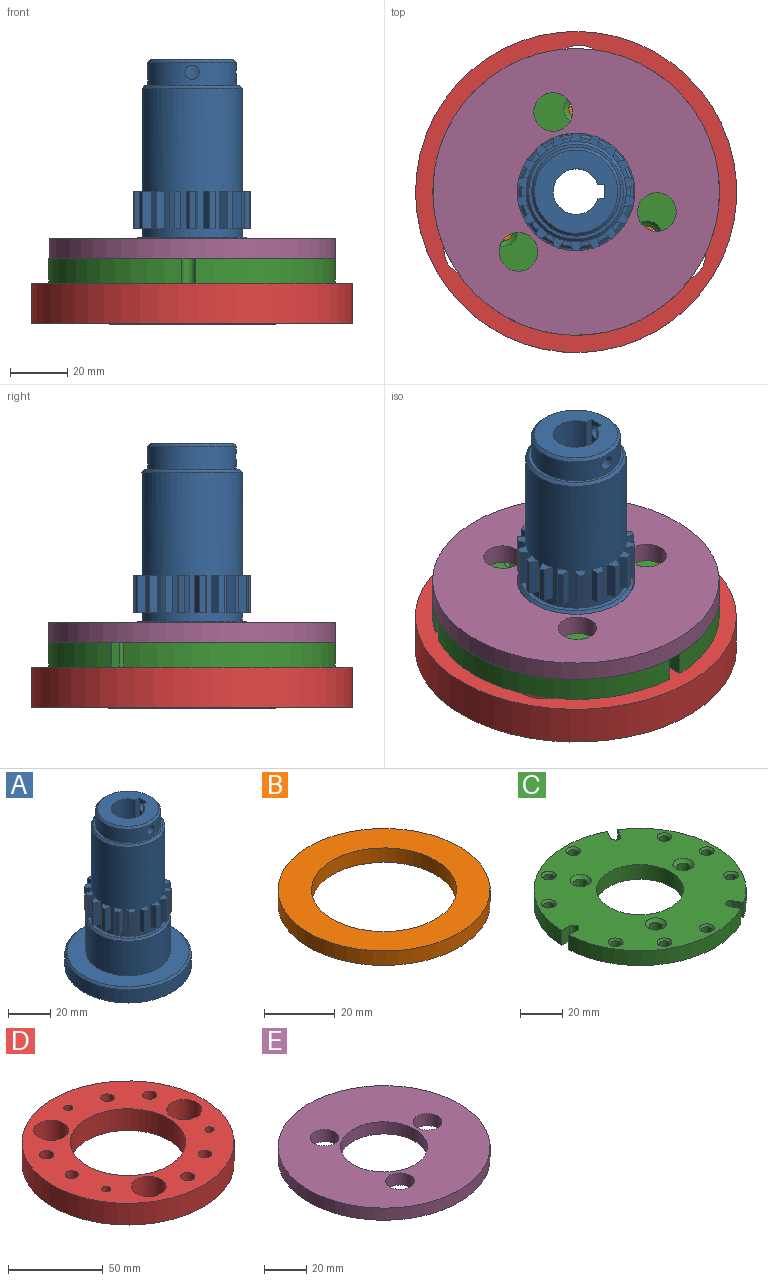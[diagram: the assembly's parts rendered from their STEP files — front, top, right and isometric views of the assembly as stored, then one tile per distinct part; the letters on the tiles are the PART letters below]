
ASSEMBLY  parts=5 mates=4
PART A: 113 faces, bbox 60x60x92.5 mm
  f0: cylinder r=15.5mm len=31mm, axis (0,0,1), area 739.9mm2, adj f4,f21,f22,f111
  f1: plane 59x5mm, normal (-1,0,0), area 285.2mm2, adj f6,f13,f14,f22
  f2: cylinder r=8mm len=63.5mm, axis (0,0,1), area 2849.1mm2, adj f5,f6,f13,f14,f21
  f3: cylinder r=17.5mm len=52mm, axis (0,0,1), area 4756.5mm2, adj f12,f16,f17,f18,f20,f23,f24,f25
  f4: plane 33x33mm, normal (0,0,1), area 100.5mm2, adj f0,f110
  f5: plane 29x29mm, normal (0,0,1), area 448.8mm2, adj f2,f13,f14,f15,f111
  f6: plane 26x26mm, normal (0,0,-1), area 319.2mm2, adj f1,f2,f7,f13,f14
  f7: cylinder r=13mm len=29mm, axis (0,0,1), area 2368.8mm2, adj f6,f8
  f8: plane 58x58mm, normal (0,0,-1), area 2111.2mm2, adj f7,f108
  f9: cylinder r=30mm len=60mm, axis (0,0,1), area 1413.7mm2, adj f108,f109
  f10: plane 58x58mm, normal (0,0,1), area 1385.4mm2, adj f11,f109
  f11: cylinder r=20mm len=40mm, axis (0,0,1), area 2513.3mm2, adj f10,f112
  f12: plane 38x38mm, normal (0,0,1), area 172mm2, adj f3,f112
  f13: plane 63.5x2.4mm, normal (0,-1,0), area 152.4mm2, adj f1,f2,f5,f6,f15
  f14: plane 63.5x2.4mm, normal (0,1,0), area 152.4mm2, adj f1,f2,f5,f6,f15
  f15: plane 5x4.5mm, normal (-1,0,0), area 12.7mm2, adj f5,f13,f14,f22
  f16: plane 4.04x3.59mm, normal (0,0,1), area 9.4mm2, adj f3,f17,f19,f20
  f17: plane 13x3.22mm, normal (0.13,-0.99,0), area 42.2mm2, adj f3,f16,f18,f19
  f18: plane 4.04x3.59mm, normal (0,0,-1), area 9.4mm2, adj f3,f17,f19,f20
  f19: cylinder r=20.5mm len=13mm, axis (0,0,-1), area 27.9mm2, adj f16,f17,f18,f20
  f20: plane 13x2.88mm, normal (0.46,0.89,0), area 42.2mm2, adj f3,f16,f18,f19
  f21: cylinder r=2.5mm len=7.9mm, axis (0,1,0), area 119.3mm2, adj f0,f2
  f22: cylinder r=2.5mm len=5.5mm, axis (-1,0,0), area 84.8mm2, adj f0,f1,f15
  f23: plane 4.25x4.24mm, normal (0,0,1), area 9.4mm2, adj f3,f24,f26,f27
  f24: plane 13x3.17mm, normal (-0.22,-0.98,0), area 42.2mm2, adj f3,f23,f25,f26
  f25: plane 4.25x4.24mm, normal (0,0,-1), area 9.4mm2, adj f3,f24,f26,f27
  f26: cylinder r=20.5mm len=13mm, axis (0,0,-1), area 27.9mm2, adj f23,f24,f25,f27
  f27: plane 13x2.39mm, normal (0.74,0.67,0), area 42.2mm2, adj f3,f23,f25,f26
  f28: plane 4.38x4.37mm, normal (0,0,1), area 9.4mm2, adj f3,f29,f31,f32
  f29: plane 13x2.74mm, normal (-0.54,-0.84,0), area 42.2mm2, adj f3,f28,f30,f31
  f30: plane 4.38x4.37mm, normal (0,0,-1), area 9.4mm2, adj f3,f29,f31,f32
  f31: cylinder r=20.5mm len=13mm, axis (0,0,-1), area 27.9mm2, adj f28,f29,f30,f32
  f32: plane 13x3mm, normal (0.92,0.38,0), area 42.2mm2, adj f3,f28,f30,f31
  f33: plane 3.99x3.97mm, normal (0,0,1), area 9.4mm2, adj f3,f34,f36,f37
  f34: plane 13x2.57mm, normal (-0.79,-0.61,0), area 42.2mm2, adj f3,f33,f35,f36
  f35: plane 3.99x3.97mm, normal (0,0,-1), area 9.4mm2, adj f3,f34,f36,f37
  f36: cylinder r=20.5mm len=13mm, axis (0,0,-1), area 27.9mm2, adj f33,f34,f35,f37
  f37: plane 13x3.24mm, normal (1,0.04,0), area 42.2mm2, adj f3,f33,f35,f36
  f38: plane 4.1x3.12mm, normal (0,0,1), area 9.4mm2, adj f3,f39,f41,f42
  f39: plane 13x3.09mm, normal (-0.95,-0.3,0), area 42.2mm2, adj f3,f38,f40,f41
  f40: plane 4.1x3.12mm, normal (0,0,-1), area 9.4mm2, adj f3,f39,f41,f42
  f41: cylinder r=20.5mm len=13mm, axis (0,0,-1), area 27.9mm2, adj f38,f39,f40,f42
  f42: plane 13x3.09mm, normal (0.95,-0.3,0), area 42.2mm2, adj f3,f38,f40,f41
  f43: plane 3.99x3.97mm, normal (0,0,1), area 9.4mm2, adj f3,f44,f46,f47
  f44: plane 13x3.24mm, normal (-1,0.04,0), area 42.2mm2, adj f3,f43,f45,f46
  f45: plane 3.99x3.97mm, normal (0,0,-1), area 9.4mm2, adj f3,f44,f46,f47
  f46: cylinder r=20.5mm len=13mm, axis (0,0,-1), area 27.9mm2, adj f43,f44,f45,f47
  f47: plane 13x2.57mm, normal (0.79,-0.61,0), area 42.2mm2, adj f3,f43,f45,f46
  f48: plane 4.38x4.37mm, normal (0,0,1), area 9.4mm2, adj f3,f49,f51,f52
  f49: plane 13x3mm, normal (-0.92,0.38,0), area 42.2mm2, adj f3,f48,f50,f51
  f50: plane 4.38x4.37mm, normal (0,0,-1), area 9.4mm2, adj f3,f49,f51,f52
  f51: cylinder r=20.5mm len=13mm, axis (0,0,-1), area 27.9mm2, adj f48,f49,f50,f52
  f52: plane 13x2.74mm, normal (0.54,-0.84,0), area 42.2mm2, adj f3,f48,f50,f51
  f53: plane 4.25x4.24mm, normal (0,0,1), area 9.4mm2, adj f3,f54,f56,f57
  f54: plane 13x2.39mm, normal (-0.74,0.67,0), area 42.2mm2, adj f3,f53,f55,f56
  f55: plane 4.25x4.24mm, normal (0,0,-1), area 9.4mm2, adj f3,f54,f56,f57
  f56: cylinder r=20.5mm len=13mm, axis (0,0,-1), area 27.9mm2, adj f53,f54,f55,f57
  f57: plane 13x3.17mm, normal (0.22,-0.98,0), area 42.2mm2, adj f3,f53,f55,f56
  f58: plane 4.04x3.59mm, normal (0,0,1), area 9.4mm2, adj f3,f59,f61,f62
  f59: plane 13x2.88mm, normal (-0.46,0.89,0), area 42.2mm2, adj f3,f58,f60,f61
  f60: plane 4.04x3.59mm, normal (0,0,-1), area 9.4mm2, adj f3,f59,f61,f62
  f61: cylinder r=20.5mm len=13mm, axis (0,0,-1), area 27.9mm2, adj f58,f59,f60,f62
  f62: plane 13x3.22mm, normal (-0.13,-0.99,0), area 42.2mm2, adj f3,f58,f60,f61
  f63: plane 4.04x3.59mm, normal (0,0,1), area 9.4mm2, adj f3,f64,f66,f67
  f64: plane 13x3.22mm, normal (-0.13,0.99,0), area 42.2mm2, adj f3,f63,f65,f66
  f65: plane 4.04x3.59mm, normal (0,0,-1), area 9.4mm2, adj f3,f64,f66,f67
  f66: cylinder r=20.5mm len=13mm, axis (0,0,-1), area 27.9mm2, adj f63,f64,f65,f67
  f67: plane 13x2.88mm, normal (-0.46,-0.89,0), area 42.2mm2, adj f3,f63,f65,f66
  f68: plane 4.25x4.24mm, normal (0,0,1), area 9.4mm2, adj f3,f69,f71,f72
  f69: plane 13x3.17mm, normal (0.22,0.98,0), area 42.2mm2, adj f3,f68,f70,f71
  f70: plane 4.25x4.24mm, normal (0,0,-1), area 9.4mm2, adj f3,f69,f71,f72
  f71: cylinder r=20.5mm len=13mm, axis (0,0,-1), area 27.9mm2, adj f68,f69,f70,f72
  f72: plane 13x2.39mm, normal (-0.74,-0.67,0), area 42.2mm2, adj f3,f68,f70,f71
  f73: plane 4.38x4.37mm, normal (0,0,1), area 9.4mm2, adj f3,f74,f76,f77
  f74: plane 13x2.74mm, normal (0.54,0.84,0), area 42.2mm2, adj f3,f73,f75,f76
  f75: plane 4.38x4.37mm, normal (0,0,-1), area 9.4mm2, adj f3,f74,f76,f77
  f76: cylinder r=20.5mm len=13mm, axis (0,0,-1), area 27.9mm2, adj f73,f74,f75,f77
  f77: plane 13x3mm, normal (-0.92,-0.38,0), area 42.2mm2, adj f3,f73,f75,f76
  f78: plane 3.99x3.97mm, normal (0,0,1), area 9.4mm2, adj f3,f79,f81,f82
  f79: plane 13x2.57mm, normal (0.79,0.61,0), area 42.2mm2, adj f3,f78,f80,f81
  f80: plane 3.99x3.97mm, normal (0,0,-1), area 9.4mm2, adj f3,f79,f81,f82
  f81: cylinder r=20.5mm len=13mm, axis (0,0,-1), area 27.9mm2, adj f78,f79,f80,f82
  f82: plane 13x3.24mm, normal (-1,-0.04,0), area 42.2mm2, adj f3,f78,f80,f81
  f83: plane 4.1x3.12mm, normal (0,0,1), area 9.4mm2, adj f3,f84,f86,f87
  f84: plane 13x3.09mm, normal (0.95,0.3,0), area 42.2mm2, adj f3,f83,f85,f86
  f85: plane 4.1x3.12mm, normal (0,0,-1), area 9.4mm2, adj f3,f84,f86,f87
  f86: cylinder r=20.5mm len=13mm, axis (0,0,-1), area 27.9mm2, adj f83,f84,f85,f87
  f87: plane 13x3.09mm, normal (-0.95,0.3,0), area 42.2mm2, adj f3,f83,f85,f86
  f88: plane 3.99x3.97mm, normal (0,0,1), area 9.4mm2, adj f3,f89,f91,f92
  f89: plane 13x3.24mm, normal (1,-0.04,0), area 42.2mm2, adj f3,f88,f90,f91
  f90: plane 3.99x3.97mm, normal (0,0,-1), area 9.4mm2, adj f3,f89,f91,f92
  f91: cylinder r=20.5mm len=13mm, axis (0,0,-1), area 27.9mm2, adj f88,f89,f90,f92
  f92: plane 13x2.57mm, normal (-0.79,0.61,0), area 42.2mm2, adj f3,f88,f90,f91
  f93: plane 4.38x4.37mm, normal (0,0,1), area 9.4mm2, adj f3,f94,f96,f97
  f94: plane 13x3mm, normal (0.92,-0.38,0), area 42.2mm2, adj f3,f93,f95,f96
  f95: plane 4.38x4.37mm, normal (0,0,-1), area 9.4mm2, adj f3,f94,f96,f97
  f96: cylinder r=20.5mm len=13mm, axis (0,0,-1), area 27.9mm2, adj f93,f94,f95,f97
  f97: plane 13x2.74mm, normal (-0.54,0.84,0), area 42.2mm2, adj f3,f93,f95,f96
  f98: plane 4.25x4.24mm, normal (0,0,1), area 9.4mm2, adj f3,f99,f101,f102
  f99: plane 13x2.39mm, normal (0.74,-0.67,0), area 42.2mm2, adj f3,f98,f100,f101
  f100: plane 4.25x4.24mm, normal (0,0,-1), area 9.4mm2, adj f3,f99,f101,f102
  f101: cylinder r=20.5mm len=13mm, axis (0,0,-1), area 27.9mm2, adj f98,f99,f100,f102
  f102: plane 13x3.17mm, normal (-0.22,0.98,0), area 42.2mm2, adj f3,f98,f100,f101
  f103: plane 4.04x3.59mm, normal (0,0,1), area 9.4mm2, adj f3,f104,f106,f107
  f104: plane 13x2.88mm, normal (0.46,-0.89,0), area 42.2mm2, adj f3,f103,f105,f106
  f105: plane 4.04x3.59mm, normal (0,0,-1), area 9.4mm2, adj f3,f104,f106,f107
  f106: cylinder r=20.5mm len=13mm, axis (0,0,-1), area 27.9mm2, adj f103,f104,f105,f107
  f107: plane 13x3.22mm, normal (0.13,0.99,0), area 42.2mm2, adj f3,f103,f105,f106
  f108: cone r=30mm half-angle=45deg, axis (0,0,1), area 262.1mm2, adj f8,f9
  f109: cone r=29mm half-angle=45deg, axis (0,0,-1), area 262.1mm2, adj f9,f10
  f110: cone r=16.5mm half-angle=45deg, axis (0,0,-1), area 151.1mm2, adj f3,f4
  f111: cone r=14.5mm half-angle=45deg, axis (0,0,-1), area 133.3mm2, adj f0,f5
  f112: cone r=19mm half-angle=45deg, axis (0,0,-1), area 173.3mm2, adj f11,f12
PART B: 4 faces, bbox 60x60x5 mm
  f0: cylinder r=30mm len=60mm, axis (0,0,1), area 942.5mm2, adj f1,f3
  f1: plane 60x60mm, normal (0,0,1), area 1507.2mm2, adj f0,f2
  f2: cylinder r=20.5mm len=41mm, axis (0,0,1), area 644mm2, adj f1,f3
  f3: plane 60x60mm, normal (0,0,-1), area 1507.2mm2, adj f0,f2
PART C: 39 faces, bbox 99.9x100x8.5 mm
  f0: cylinder r=3.25mm len=7.02mm, axis (0,0,-1), area 143.4mm2, adj f6,f29
  f1: cylinder r=3.25mm len=7.02mm, axis (0,0,-1), area 143.4mm2, adj f6,f28
  f2: cylinder r=3.25mm len=7.02mm, axis (0,0,-1), area 143.4mm2, adj f6,f27
  f3: cylinder r=50mm len=72.74mm, axis (0,0,1), area 847.6mm2, adj f6,f7,f12,f15
  f4: cylinder r=50mm len=83.99mm, axis (0,0,1), area 847.6mm2, adj f6,f7,f9,f13
  f5: cylinder r=50mm len=72.74mm, axis (0,0,1), area 847.6mm2, adj f6,f7,f10,f14
  f6: plane 100x99.94mm, normal (0,0,-1), area 6145.8mm2, adj f0,f1,f2,f3,f4,f5,f8,f9
  f7: plane 100x99.94mm, normal (0,0,1), area 5840.1mm2, adj f3,f4,f5,f8,f9,f10,f12,f13
  f8: cylinder r=20.5mm len=41mm, axis (0,0,1), area 1094.8mm2, adj f6,f7
  f9: plane 8.5x4.71mm, normal (-0.87,0.5,0), area 46.2mm2, adj f4,f6,f7,f25
  f10: plane 8.5x4.71mm, normal (0.87,-0.5,0), area 46.2mm2, adj f5,f6,f7,f25
  f11: cylinder r=2.5mm len=7.5mm, axis (0,0,-1), area 117.8mm2, adj f6,f37
  f12: plane 8.5x4.71mm, normal (0.87,0.5,0), area 46.2mm2, adj f3,f6,f7,f17
  f13: plane 8.5x4.71mm, normal (-0.87,-0.5,0), area 46.2mm2, adj f4,f6,f7,f17
  f14: plane 8.5x5.44mm, normal (0,-1,0), area 46.2mm2, adj f5,f6,f7,f21
  f15: plane 8.5x5.44mm, normal (0,1,0), area 46.2mm2, adj f3,f6,f7,f21
  f16: cylinder r=2.5mm len=7.5mm, axis (0,0,-1), area 117.8mm2, adj f6,f38
  f17: cylinder r=2.5mm len=8.5mm, axis (0,0,-1), area 66.8mm2, adj f6,f7,f12,f13
  f18: cylinder r=2.5mm len=7.5mm, axis (0,0,-1), area 117.8mm2, adj f6,f35
  f19: cylinder r=2.5mm len=7.5mm, axis (0,0,-1), area 117.8mm2, adj f6,f34
  f20: cylinder r=2.5mm len=7.5mm, axis (0,0,-1), area 117.8mm2, adj f6,f33
  f21: cylinder r=2.5mm len=8.5mm, axis (0,0,-1), area 66.8mm2, adj f6,f7,f14,f15
  f22: cylinder r=2.5mm len=7.5mm, axis (0,0,-1), area 117.8mm2, adj f6,f32
  f23: cylinder r=2.5mm len=7.5mm, axis (0,0,-1), area 117.8mm2, adj f6,f31
  f24: cylinder r=2.5mm len=7.5mm, axis (0,0,-1), area 117.8mm2, adj f6,f30
  f25: cylinder r=2.5mm len=8.5mm, axis (0,0,-1), area 66.8mm2, adj f6,f7,f9,f10
  f26: cylinder r=2.5mm len=7.5mm, axis (0,0,-1), area 117.8mm2, adj f6,f36
  f27: sphere r=6.5mm, area 60.3mm2, adj f2,f7
  f28: sphere r=6.5mm, area 60.3mm2, adj f1,f7
  f29: sphere r=6.5mm, area 60.3mm2, adj f0,f7
  f30: cone r=3.5mm half-angle=45deg, axis (0,0,1), area 26.7mm2, adj f7,f24
  f31: cone r=3.5mm half-angle=45deg, axis (0,0,1), area 26.7mm2, adj f7,f23
  f32: cone r=3.5mm half-angle=45deg, axis (0,0,1), area 26.7mm2, adj f7,f22
  f33: cone r=3.5mm half-angle=45deg, axis (0,0,1), area 26.7mm2, adj f7,f20
  f34: cone r=3.5mm half-angle=45deg, axis (0,0,1), area 26.7mm2, adj f7,f19
  f35: cone r=3.5mm half-angle=45deg, axis (0,0,1), area 26.7mm2, adj f7,f18
  f36: cone r=3.5mm half-angle=45deg, axis (0,0,1), area 26.7mm2, adj f7,f26
  f37: cone r=3.5mm half-angle=45deg, axis (0,0,1), area 26.7mm2, adj f7,f11
  f38: cone r=3.5mm half-angle=45deg, axis (0,0,1), area 26.7mm2, adj f7,f16
PART D: 16 faces, bbox 112x112x14 mm
  f0: plane 112x112mm, normal (0,0,1), area 5820.9mm2, adj f1,f3,f4,f5,f6,f7,f8,f9
  f1: cylinder r=30.5mm len=61mm, axis (0,0,1), area 2682.9mm2, adj f0,f2
  f2: plane 112x112mm, normal (0,0,-1), area 5820.9mm2, adj f1,f3,f4,f5,f6,f7,f8,f9
  f3: cylinder r=56mm len=112mm, axis (0,0,1), area 4926mm2, adj f0,f2
  f4: cylinder r=3.5mm len=14mm, axis (0,0,-1), area 307.9mm2, adj f0,f2
  f5: cylinder r=3.75mm len=14mm, axis (0,0,-1), area 329.9mm2, adj f0,f2
  f6: cylinder r=9.25mm len=18.5mm, axis (0,0,-1), area 813.7mm2, adj f0,f2
  f7: cylinder r=2.4mm len=14mm, axis (0,0,-1), area 211.1mm2, adj f0,f2
  f8: cylinder r=3.5mm len=14mm, axis (0,0,-1), area 307.9mm2, adj f0,f2
  f9: cylinder r=3.75mm len=14mm, axis (0,0,-1), area 329.9mm2, adj f0,f2
  f10: cylinder r=9.25mm len=18.5mm, axis (0,0,-1), area 813.7mm2, adj f0,f2
  f11: cylinder r=2.4mm len=14mm, axis (0,0,-1), area 211.1mm2, adj f0,f2
  f12: cylinder r=3.5mm len=14mm, axis (0,0,-1), area 307.9mm2, adj f0,f2
  f13: cylinder r=3.75mm len=14mm, axis (0,0,-1), area 329.9mm2, adj f0,f2
  f14: cylinder r=9.25mm len=18.5mm, axis (0,0,-1), area 813.7mm2, adj f0,f2
  f15: cylinder r=2.4mm len=14mm, axis (0,0,-1), area 211.1mm2, adj f0,f2
PART E: 7 faces, bbox 100x100x7 mm
  f0: cylinder r=20.5mm len=41mm, axis (0,0,1), area 901.6mm2, adj f1,f3
  f1: plane 100x100mm, normal (0,0,-1), area 6104.3mm2, adj f0,f2,f4,f5,f6
  f2: cylinder r=50mm len=100mm, axis (0,0,1), area 2199.1mm2, adj f1,f3
  f3: plane 100x100mm, normal (0,0,1), area 6104.3mm2, adj f0,f2,f4,f5,f6
  f4: cylinder r=6.75mm len=13.5mm, axis (0,0,-1), area 296.9mm2, adj f1,f3
  f5: cylinder r=6.75mm len=13.5mm, axis (0,0,-1), area 296.9mm2, adj f1,f3
  f6: cylinder r=6.75mm len=13.5mm, axis (0,0,-1), area 296.9mm2, adj f1,f3
PLACE A t=(-45.95,-40.57,52.46)mm fixed
PLACE B t=(-45.95,-40.57,52.46)mm
PLACE C rot(axis=(0,0,-1),31.4deg) t=(-45.95,-40.57,52.46)mm
PLACE D rot(axis=(0,0,-1),31.4deg) t=(-45.95,-40.57,52.46)mm
PLACE E rot(axis=(0,0,1),106.1deg) t=(-45.95,-40.57,52.46)mm
MATE fastened C.f3 <-> D.f1  axis (0,0,-1) through (-45.95,-40.57,77.46)mm
MATE fastened A.f19 <-> B.f0  axis (0,0,1) through (-45.95,-40.57,72.46)mm
MATE revolute B.f0 <-> C.f3  axis (0,0,1) through (-45.95,-40.57,77.46)mm
MATE revolute C.f3 <-> E.f0  axis (0,0,1) through (-45.95,-40.57,85.96)mm
